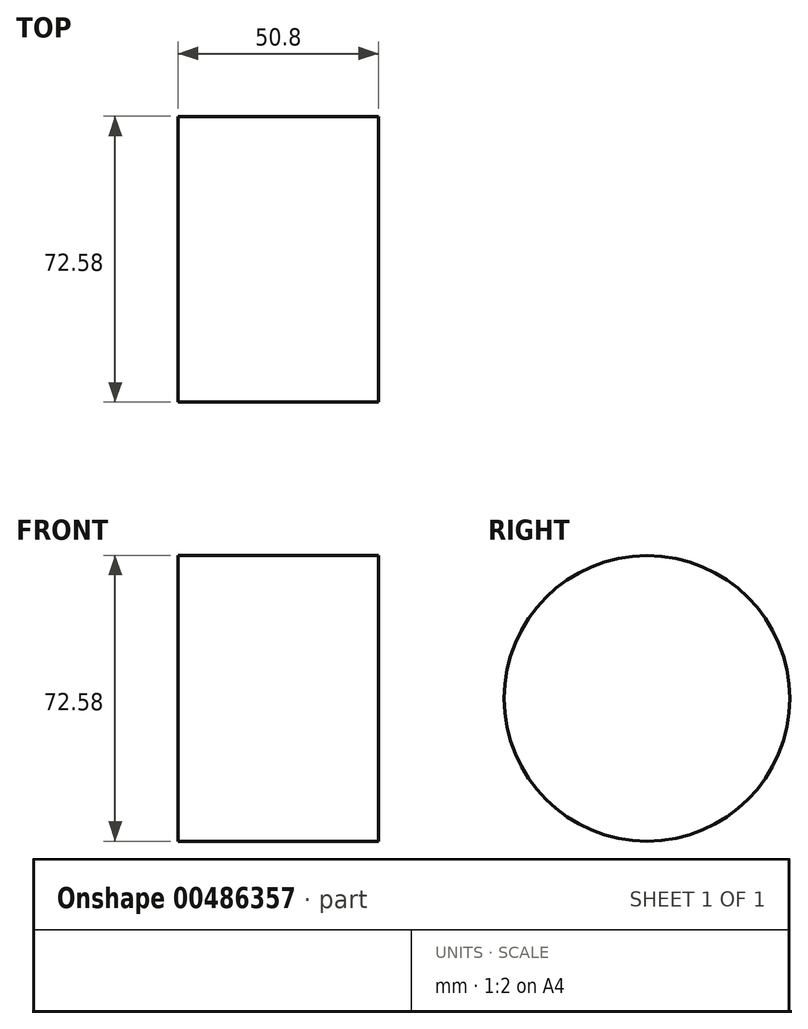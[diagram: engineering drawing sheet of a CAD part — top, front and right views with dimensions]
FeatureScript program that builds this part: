
annotation { "Feature Type Name" : "Feature", "Feature Type Description" : "" }
export const myFeature = defineFeature(function(context is Context, id is Id, definition is map)
    precondition{}
    {
        {
            var Q0;
            Q0=qCreatedBy(makeId("Right.planeOp"),FACE);
            var sketch = newSketch(context, id + "F0", { "sketchPlane" : qUnion([Q0])});
            skCircle(sketch, "E0", {"center": v(0, 0) * mm, "radius": 36.29 * mm});
            skSolve(sketch);
        }
        {
            var Q0;
            Q0 = qSketchRegion(id + "F0", true);
            extrude(context, id + "F1", {"entities" : qUnion([Q0]), "depth" : 25.4 * mm});
        }
        {
            var Q0;
            Q0=makeQuery(id+"F1.opExtrude","CAP_FACE",FACE,{"disambiguationData":[OSD([sQuery(id+"F0.wireOp",EDGE,"E0")])],"isStart":false});
            var sketch = newSketch(context, id + "F2", { "sketchPlane" : qUnion([Q0])});
            skCircle(sketch, "E1", {"center": v(0, -0.94) * mm, "radius": 24.67 * mm});
            skSolve(sketch);
        }
        {
            var Q0;
            Q0 = qSketchRegion(id + "F0", true);
            extrude(context, id + "F3", {"entities" : qUnion([Q0]), "depth" : 25.4 * mm});
        }
        {
            var Q0;
            Q0=makeQuery(id+"F3.opExtrude","CAP_FACE",FACE,{"disambiguationData":[OSD([sQuery(id+"F0.wireOp",EDGE,"E0")])],"isStart":false});
            extrude(context, id + "F4", {"entities" : qUnion([Q0]), "operationType" : NewBodyOperationType.ADD, "depth" : 25.4 * mm});
        }
        {
            var Q0;
            Q0=makeQuery(id+"F4.opExtrude","CAP_FACE",FACE,{"disambiguationData":[OSD([sQuery(id+"F0.wireOp",EDGE,"E0")])],"isStart":false});
            extrude(context, id + "F5", {"entities" : qUnion([Q0]), "operationType" : NewBodyOperationType.ADD, "oppositeDirection" : true, "depth" : 25.4 * mm});
        }
        {
            var Q0;
            Q0=makeQuery(id+"F4.opExtrude","CAP_FACE",FACE,{"disambiguationData":[OSD([sQuery(id+"F0.wireOp",EDGE,"E0")])],"isStart":false});
            var Q1;
            Q1=makeQuery(id+"F2.imprint","IMPRINT",FACE,{"disambiguationData":[TD([[makeQuery(id+"F2.imprint","IMPRINT",EDGE,{"derivedFrom":sQuery(id+"F2.wireOp",EDGE,"E1")}),1.0]])]});
            extrude(context, id + "F6", {"entities" : qUnion([Q0, Q1]), "operationType" : NewBodyOperationType.ADD, "oppositeDirection" : true, "depth" : 25.4 * mm});
        }
        {
            var Q0;
            Q0=makeQuery(id+"F4.opExtrude","CAP_FACE",FACE,{"disambiguationData":[OSD([sQuery(id+"F0.wireOp",EDGE,"E0")])],"isStart":false});
            extrude(context, id + "F7", {"entities" : qUnion([Q0]), "operationType" : NewBodyOperationType.ADD, "oppositeDirection" : true, "depth" : 25.4 * mm});
        }
        {
            var Q0;
            Q0=makeQuery(id+"F4.opExtrude","CAP_FACE",FACE,{"disambiguationData":[OSD([sQuery(id+"F0.wireOp",EDGE,"E0")])],"isStart":false});
            extrude(context, id + "F8", {"entities" : qUnion([Q0]), "operationType" : NewBodyOperationType.ADD, "oppositeDirection" : true, "depth" : 25.4 * mm});
        }
    });
